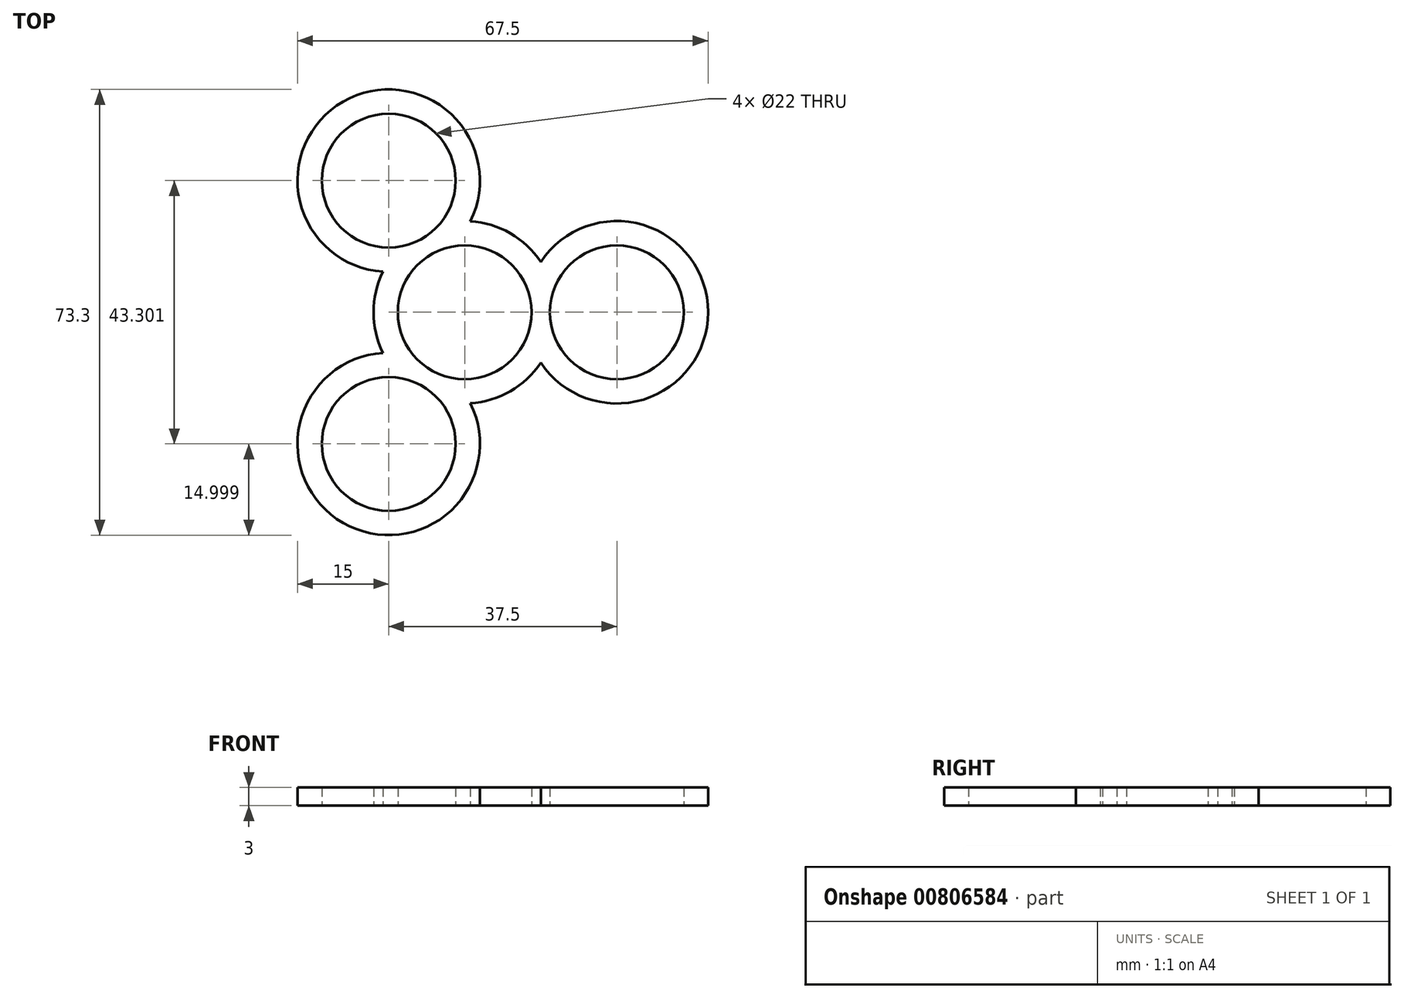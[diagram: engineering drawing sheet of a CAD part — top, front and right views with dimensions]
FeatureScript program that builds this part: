
annotation { "Feature Type Name" : "Feature", "Feature Type Description" : "" }
export const myFeature = defineFeature(function(context is Context, id is Id, definition is map)
    precondition{}
    {
        {
            var Q0;
            Q0=qCreatedBy(makeId("Top.planeOp"),FACE);
            var sketch = newSketch(context, id + "F0", { "sketchPlane" : qUnion([Q0])});
            skArc(sketch, "E0", {"start": v(5.54, -9.5) * mm, "mid": v(10.92, 1.34) * mm, "end": v(3.08, 10.56) * mm});
            skArc(sketch, "E1", {"start": v(7.55, -12.96) * mm, "mid": v(10.3, -10.9) * mm, "end": v(12.5, -8.3) * mm});
            skLineSegment(sketch, "E2", {"start": v(11, 0) * mm, "end": v(14, 0) * mm});
            skCircle(sketch, "E3", {"center": v(25, 0) * mm, "radius": 11 * mm});
            skArc(sketch, "E4", {"start": v(12.5, -8.3) * mm, "mid": v(40, 0) * mm, "end": v(12.5, 8.3) * mm});
            skArc(sketch, "E5.trimOffspring", {"start": v(12.5, 8.3) * mm, "mid": v(8.9, 12.08) * mm, "end": v(4.2, 14.4) * mm});
            skArc(sketch, "E6.1.0", {"start": v(0.93, 14.97) * mm, "mid": v(-20, 34.64) * mm, "end": v(-13.43, 6.68) * mm});
            skCircle(sketch, "E6.1.1", {"center": v(-12.5, 21.65) * mm, "radius": 11 * mm});
            skArc(sketch, "E6.1.2", {"start": v(5.46, 9.55) * mm, "mid": v(-6.62, 8.79) * mm, "end": v(-10.68, -2.61) * mm});
            skArc(sketch, "E6.1.3", {"start": v(7.45, 13.02) * mm, "mid": v(4.3, 14.37) * mm, "end": v(0.93, 14.97) * mm});
            skArc(sketch, "E6.1.4", {"start": v(-13.43, 6.68) * mm, "mid": v(-14.9, 1.66) * mm, "end": v(-14.57, -3.56) * mm});
            skArc(sketch, "E6.2.0", {"start": v(-13.43, -6.68) * mm, "mid": v(-20, -34.64) * mm, "end": v(0.93, -14.97) * mm});
            skCircle(sketch, "E6.2.1", {"center": v(-12.5, -21.65) * mm, "radius": 11 * mm});
            skArc(sketch, "E6.2.2", {"start": v(-11, -0.05) * mm, "mid": v(-4.3, -10.13) * mm, "end": v(7.6, -7.95) * mm});
            skArc(sketch, "E6.2.3", {"start": v(-15, -0.06) * mm, "mid": v(-14.6, -3.46) * mm, "end": v(-13.43, -6.68) * mm});
            skArc(sketch, "E6.2.4", {"start": v(0.93, -14.97) * mm, "mid": v(6.02, -13.74) * mm, "end": v(10.37, -10.84) * mm});
            skSolve(sketch);
        }
        {
            var Q0;
            Q0 = qSketchRegion(id + "F0", true);
            extrude(context, id + "F1", {"entities" : qUnion([Q0]), "depth" : 3 * mm, "offsetDistance" : 25 * mm});
        }
    });
